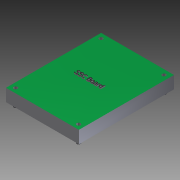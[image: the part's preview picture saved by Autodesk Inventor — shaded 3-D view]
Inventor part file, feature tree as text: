
AUTODESK INVENTOR PART (.ipt)
format: ipt  version: 2012 (Build 160160000, 160)  size: 333,824 bytes
history: native  units: mm
features: extrude x5, thread x4, sketch x1, emboss x1
ambient origin geometry x8: Origin, YZ Plane, XZ Plane, XY Plane, X Axis, Y Axis, Z Axis, Center Point
bodies: Solid1 (feature_tree)
feature tree (11):
  sketch  "Sketch1"  dims[d21=3.0mm d24=3.0mm d27=3.0mm d30=3.0mm d31=0.0mm d32=3.0mm d33=0.0mm d34=3.0mm d35=0.0mm d36=10.0mm d37=0.0mm d41=1.0mm d42=0.0mm d43=10.0mm d44=0.0mm d45=10.0mm d46=0.0mm d47=10.0mm d48=0.0mm d49=10.0mm d50=0.0mm d51=10.0mm d52=0.0mm d53=58.44mm d54=76.3mm d55=50.55mm d56=68.5mm d57=68.5mm d58=50.55mm]
  extrude  "Extrusion4"  Depth=3.0mm
  extrude  "Extrusion5"  Depth=3.0mm
  extrude  "Extrusion6"  Depth=3.0mm TaperAngle=0.0deg
  extrude  "Extrusion7"  Depth=3.0mm TaperAngle=0.0deg
  emboss  "Emboss1"
  extrude  "Extrusion8"  Depth=3.0mm TaperAngle=0.0deg
  thread  "Thread1"  [1 undecoded]
  thread  "Thread2"  [1 undecoded]
  thread  "Thread3"  [1 undecoded]
  thread  "Thread4"  [1 undecoded]
note: 4 required parameter values undecoded (feature->parameter linkage not recoverable at this tier; creation-order binding heuristic only, values carry confidence <= 0.55)
